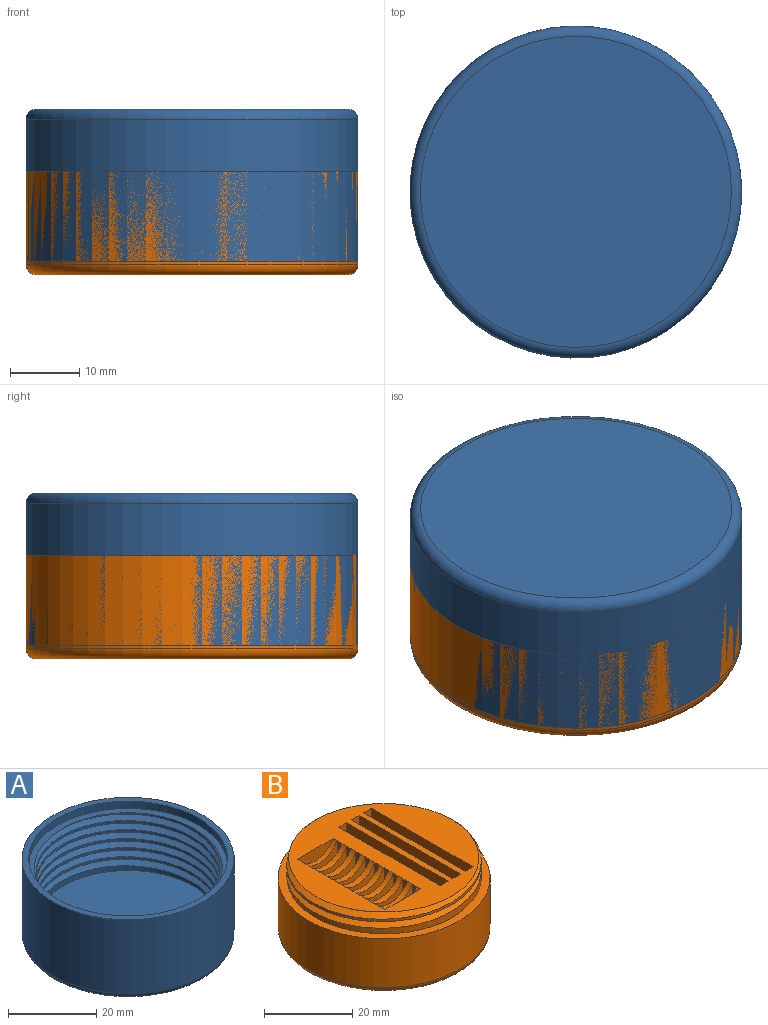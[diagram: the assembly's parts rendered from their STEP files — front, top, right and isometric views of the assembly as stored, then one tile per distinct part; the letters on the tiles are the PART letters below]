
ASSEMBLY  parts=2 mates=1
PART A: 11 faces, bbox 53.1x53.1x23.2 mm
  f0: cylinder r=20.8mm len=41.6mm, axis (0,0,-1), area 610.7mm2, adj f1,f2,f3,f4,f5
  f1: plane 46.15x46.15mm, normal (0,0,1), area 156.1mm2, adj f0,f4,f5,f6
  f2: plane 41.6x41.6mm, normal (0,0,1), area 1359.2mm2, adj f0
  f3: plane 1.8x1.27mm, normal (0.59,-0.81,0), area 1.4mm2, adj f0,f4,f5
  f4: bspline ~51.64x44.72mm, area 1518.4mm2, adj f0,f1,f3,f5
  f5: bspline ~51.64x44.72mm, area 1431.1mm2, adj f0,f1,f3,f4
  f6: cylinder r=22.5mm len=45mm, axis (0,0,-1), area 282.7mm2, adj f1,f7
  f7: plane 48x48mm, normal (0,0,1), area 219.1mm2, adj f6,f10
  f8: plane 45x45mm, normal (0,0,-1), area 1590.4mm2, adj f9
  f9: torus R=22.5mm, axis (0,0,1), area 347.2mm2, adj f8,f10
  f10: cylinder r=24mm len=48mm, axis (0,0,-1), area 3091.3mm2, adj f7,f9
PART B: 81 faces, bbox 52x52x21 mm
  f0: plane 43.06x42.93mm, normal (0,0,1), area 879mm2, adj f1,f6,f7,f9,f11,f14,f16,f19
  f1: cylinder r=22mm len=44mm, axis (0,0,-1), area 283.2mm2, adj f0,f3,f5,f6,f7
  f2: cylinder r=24mm len=48mm, axis (0,0,-1), area 2035.8mm2, adj f3,f68
  f3: plane 48x48mm, normal (0,0,1), area 289mm2, adj f1,f2
  f4: plane 45x45mm, normal (0,0,-1), area 1590.4mm2, adj f68
  f5: plane 1.8x1.56mm, normal (0,1,0), area 1.4mm2, adj f1,f6,f7
  f6: bspline ~50.81x44mm, area 437.5mm2, adj f0,f1,f5,f7
  f7: bspline ~50.81x44mm, area 350mm2, adj f0,f1,f5,f6
  f8: plane 11.5x11mm, normal (0,1,0), area 98.9mm2, adj f9,f11,f12,f79
  f9: plane 11x1.5mm, normal (-1,0,0), area 16.5mm2, adj f0,f8,f10,f12
  f10: plane 11.5x11mm, normal (0,-1,0), area 98.9mm2, adj f9,f11,f12,f78
  f11: plane 11x1.5mm, normal (1,0,0), area 16.5mm2, adj f0,f8,f10,f12
  f12: plane 11.5x1.5mm, normal (0,0,1), area 17.2mm2, adj f8,f9,f10,f11
  f13: plane 11.5x11mm, normal (0,1,0), area 98.9mm2, adj f14,f16,f17,f78
  f14: plane 11x1.5mm, normal (-1,0,0), area 16.5mm2, adj f0,f13,f15,f17
  f15: plane 11.5x11mm, normal (0,-1,0), area 98.9mm2, adj f14,f16,f17,f77
  f16: plane 11x1.5mm, normal (1,0,0), area 16.5mm2, adj f0,f13,f15,f17
  f17: plane 11.5x1.5mm, normal (0,0,1), area 17.2mm2, adj f13,f14,f15,f16
  f18: plane 11.5x11mm, normal (0,1,0), area 98.9mm2, adj f19,f21,f22,f77
  f19: plane 11x1.5mm, normal (-1,0,0), area 16.5mm2, adj f0,f18,f20,f22
  f20: plane 11.5x11mm, normal (0,-1,0), area 98.9mm2, adj f19,f21,f22,f76
  f21: plane 11x1.5mm, normal (1,0,0), area 16.5mm2, adj f0,f18,f20,f22
  f22: plane 11.5x1.5mm, normal (0,0,1), area 17.2mm2, adj f18,f19,f20,f21
  f23: plane 11x1.5mm, normal (-1,0,0), area 16.5mm2, adj f0,f24,f26,f27
  f24: plane 11.5x11mm, normal (0,-1,0), area 98.9mm2, adj f23,f25,f27,f75
  f25: plane 11x1.5mm, normal (1,0,0), area 16.5mm2, adj f0,f24,f26,f27
  f26: plane 11.5x11mm, normal (0,1,0), area 98.9mm2, adj f23,f25,f27,f76
  f27: plane 11.5x1.5mm, normal (0,0,1), area 17.2mm2, adj f23,f24,f25,f26
  f28: plane 11.5x11mm, normal (0,1,0), area 98.9mm2, adj f29,f31,f32,f75
  f29: plane 11x1.5mm, normal (-1,0,0), area 16.5mm2, adj f0,f28,f30,f32
  f30: plane 11.5x11mm, normal (0,-1,0), area 98.9mm2, adj f29,f31,f32,f74
  f31: plane 11x1.5mm, normal (1,0,0), area 16.5mm2, adj f0,f28,f30,f32
  f32: plane 11.5x1.5mm, normal (0,0,1), area 17.2mm2, adj f28,f29,f30,f31
  f33: plane 11.5x11mm, normal (0,1,0), area 98.9mm2, adj f34,f36,f37,f74
  f34: plane 11x1.5mm, normal (-1,0,0), area 16.5mm2, adj f0,f33,f35,f37
  f35: plane 11.5x11mm, normal (0,-1,0), area 98.9mm2, adj f34,f36,f37,f73
  f36: plane 11x1.5mm, normal (1,0,0), area 16.5mm2, adj f0,f33,f35,f37
  f37: plane 11.5x1.5mm, normal (0,0,1), area 17.2mm2, adj f33,f34,f35,f36
  f38: plane 11.5x11mm, normal (0,1,0), area 98.9mm2, adj f39,f41,f42,f73
  f39: plane 11x1.5mm, normal (-1,0,0), area 16.5mm2, adj f0,f38,f40,f42
  f40: plane 11.5x11mm, normal (0,-1,0), area 98.9mm2, adj f39,f41,f42,f72
  f41: plane 11x1.5mm, normal (1,0,0), area 16.5mm2, adj f0,f38,f40,f42
  f42: plane 11.5x1.5mm, normal (0,0,1), area 17.2mm2, adj f38,f39,f40,f41
  f43: plane 11.5x11mm, normal (0,1,0), area 98.9mm2, adj f44,f46,f47,f72
  f44: plane 11x1.5mm, normal (-1,0,0), area 16.5mm2, adj f0,f43,f45,f47
  f45: plane 11.5x11mm, normal (0,-1,0), area 98.9mm2, adj f44,f46,f47,f71
  f46: plane 11x1.5mm, normal (1,0,0), area 16.5mm2, adj f0,f43,f45,f47
  f47: plane 11.5x1.5mm, normal (0,0,1), area 17.2mm2, adj f43,f44,f45,f46
  f48: plane 11.5x11mm, normal (0,1,0), area 98.9mm2, adj f49,f51,f52,f71
  f49: plane 11x1.5mm, normal (-1,0,0), area 16.5mm2, adj f0,f48,f50,f52
  f50: plane 11.5x11mm, normal (0,-1,0), area 98.9mm2, adj f49,f51,f52,f69
  f51: plane 11x1.5mm, normal (1,0,0), area 16.5mm2, adj f0,f48,f50,f52
  f52: plane 11.5x1.5mm, normal (0,0,1), area 17.2mm2, adj f48,f49,f50,f51
  f53: plane 32.5x18mm, normal (1,0,0), area 585mm2, adj f0,f54,f56,f57
  f54: plane 18x2.5mm, normal (0,1,0), area 45mm2, adj f0,f53,f55,f57
  f55: plane 32.5x18mm, normal (-1,0,0), area 585mm2, adj f0,f54,f56,f57
  f56: plane 18x2.5mm, normal (0,-1,0), area 45mm2, adj f0,f53,f55,f57
  f57: plane 32.5x2.5mm, normal (0,0,1), area 81.3mm2, adj f53,f54,f55,f56
  f58: plane 32.5x18mm, normal (1,0,0), area 585mm2, adj f0,f59,f61,f62
  f59: plane 18x2.5mm, normal (0,1,0), area 45mm2, adj f0,f58,f60,f62
  f60: plane 32.5x18mm, normal (-1,0,0), area 585mm2, adj f0,f59,f61,f62
  f61: plane 18x2.5mm, normal (0,-1,0), area 45mm2, adj f0,f58,f60,f62
  f62: plane 32.5x2.5mm, normal (0,0,1), area 81.3mm2, adj f58,f59,f60,f61
  f63: plane 32.5x18mm, normal (1,0,0), area 585mm2, adj f0,f64,f66,f67
  f64: plane 18x2.5mm, normal (0,1,0), area 45mm2, adj f0,f63,f65,f67
  f65: plane 32.5x18mm, normal (-1,0,0), area 585mm2, adj f0,f64,f66,f67
  f66: plane 18x2.5mm, normal (0,-1,0), area 45mm2, adj f0,f63,f65,f67
  f67: plane 32.5x2.5mm, normal (0,0,1), area 81.3mm2, adj f63,f64,f65,f66
  f68: torus R=22.5mm, axis (0,0,1), area 347.2mm2, adj f2,f4
  f69: cylinder r=6.58mm len=11.5mm, axis (0,1,0), area 17.5mm2, adj f0,f50,f70
  f70: plane 11.5x3.38mm, normal (0,-1,0), area 27.6mm2, adj f0,f69
  f71: cylinder r=6.58mm len=11.5mm, axis (0,1,0), area 21mm2, adj f0,f45,f48
  f72: cylinder r=6.58mm len=11.5mm, axis (0,1,0), area 21mm2, adj f0,f40,f43
  f73: cylinder r=6.58mm len=11.5mm, axis (0,1,0), area 21mm2, adj f0,f35,f38
  f74: cylinder r=6.58mm len=11.5mm, axis (0,1,0), area 21mm2, adj f0,f30,f33
  f75: cylinder r=6.58mm len=11.5mm, axis (0,1,0), area 21mm2, adj f0,f24,f28
  f76: cylinder r=6.58mm len=11.5mm, axis (0,1,0), area 21mm2, adj f0,f20,f26
  f77: cylinder r=6.58mm len=11.5mm, axis (0,1,0), area 21mm2, adj f0,f15,f18
  f78: cylinder r=6.58mm len=11.5mm, axis (0,1,0), area 21mm2, adj f0,f10,f13
  f79: cylinder r=6.58mm len=11.5mm, axis (0,1,0), area 17.5mm2, adj f0,f8,f80
  f80: plane 11.5x3.38mm, normal (0,1,0), area 27.6mm2, adj f0,f79
PLACE A rot(axis=(-1,0,0),180deg) t=(4,-5.54,45.01)mm
PLACE B rot(axis=(0.03,1,0.03),0deg) t=(4,-5.54,21.01)mm
MATE cylindrical A.f0 <-> B.f1  axis (0,0,-1) through (4,-5.54,41.01)mm
